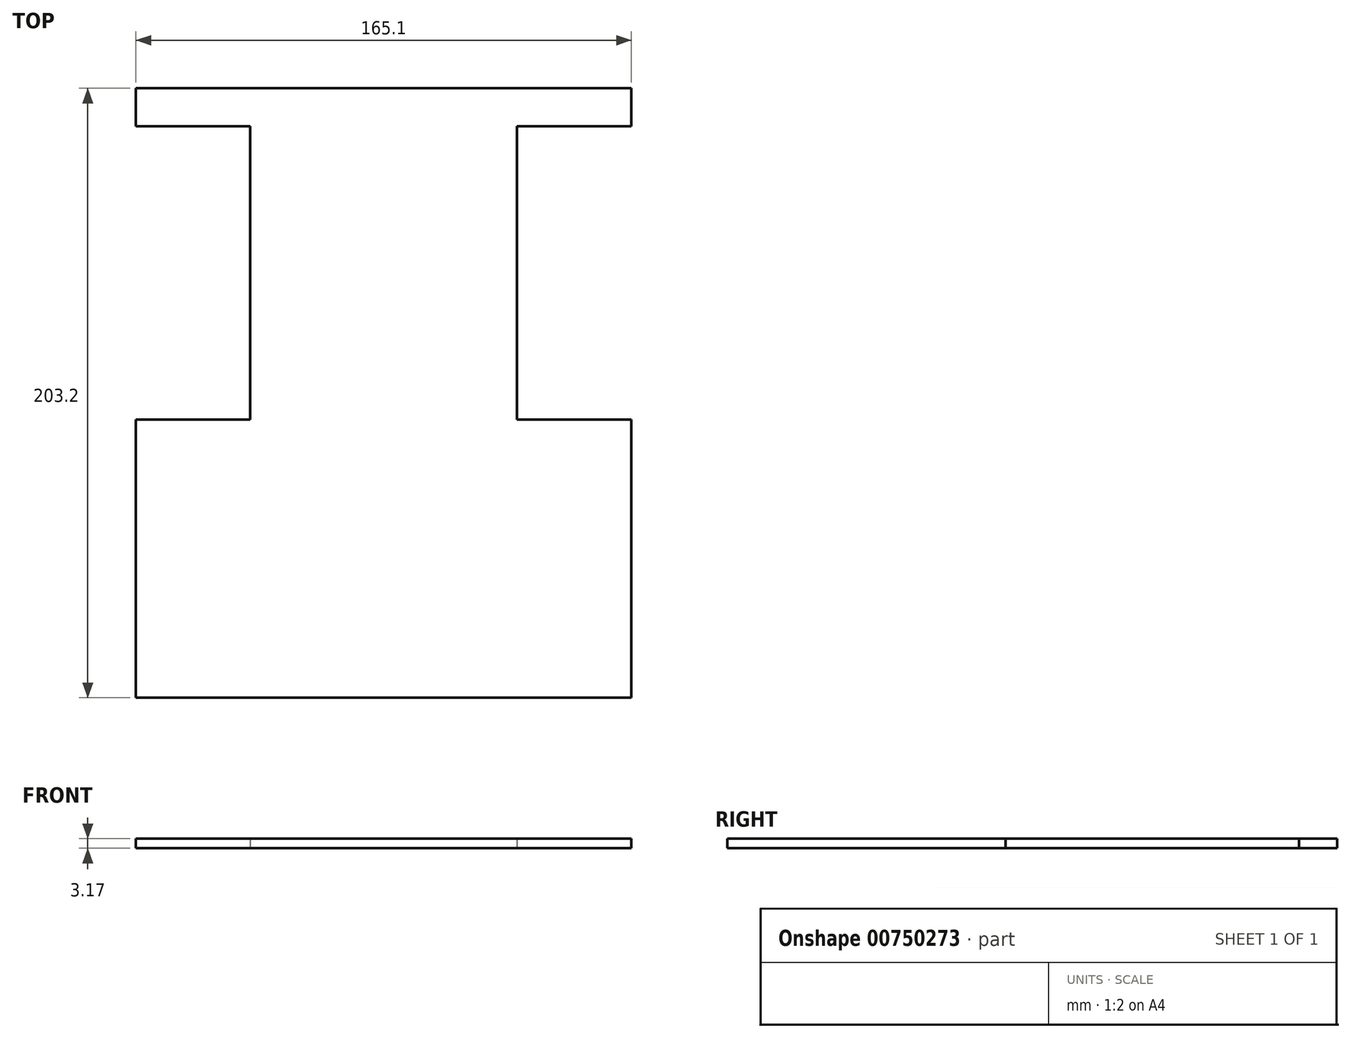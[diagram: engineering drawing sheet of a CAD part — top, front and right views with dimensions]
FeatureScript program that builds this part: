
annotation { "Feature Type Name" : "Feature", "Feature Type Description" : "" }
export const myFeature = defineFeature(function(context is Context, id is Id, definition is map)
    precondition{}
    {
        {
            var Q0;
            Q0=qCreatedBy(makeId("Top.planeOp"),FACE);
            var sketch = newSketch(context, id + "F0", { "sketchPlane" : qUnion([Q0])});
            skLineSegment(sketch, "E0", {"start": v(-55.1, 58.7) * mm, "end": v(-38.1, 58.7) * mm});
            skLineSegment(sketch, "E1", {"start": v(-38.1, 58.7) * mm, "end": v(-38.1, -21.3) * mm});
            skLineSegment(sketch, "E2", {"start": v(-38.1, -21.3) * mm, "end": v(-55.1, -21.3) * mm});
            skLineSegment(sketch, "E3", {"start": v(-55.1, -21.3) * mm, "end": v(-55.1, 58.7) * mm});
            skLineSegment(sketch, "E4", {"start": v(-38.1, 51.4) * mm, "end": v(-38.1, -46.4) * mm});
            skLineSegment(sketch, "E5", {"start": v(-38.1, -46.4) * mm, "end": v(0, -46.4) * mm});
            skLineSegment(sketch, "E6", {"start": v(-38.1, 51.4) * mm, "end": v(0, 51.4) * mm});
            skLineSegment(sketch, "E7", {"start": v(0, 51.4) * mm, "end": v(0, -46.4) * mm});
            skLineSegment(sketch, "E8", {"start": v(-38.1, 58.7) * mm, "end": v(-38.1, 18.7) * mm});
            skLineSegment(sketch, "E9", {"start": v(-38.1, 51.4) * mm, "end": v(-38.1, 18.7) * mm});
            skLineSegment(sketch, "E10", {"start": v(0, 24.96) * mm, "end": v(17, 24.96) * mm});
            skLineSegment(sketch, "E11", {"start": v(17, 24.96) * mm, "end": v(17, 1.94) * mm});
            skLineSegment(sketch, "E12", {"start": v(17, 1.94) * mm, "end": v(0, 1.94) * mm});
            skLineSegment(sketch, "E13", {"start": v(0, 1.94) * mm, "end": v(0, 24.96) * mm});
            skLineSegment(sketch, "E14.MirrorCS", {"start": v(127, 58.7) * mm, "end": v(127, 18.7) * mm});
            skLineSegment(sketch, "E15.MirrorCS", {"start": v(88.9, 24.96) * mm, "end": v(71.9, 24.96) * mm});
            skLineSegment(sketch, "E16.MirrorCS", {"start": v(127, 51.4) * mm, "end": v(127, 18.7) * mm});
            skLineSegment(sketch, "E17.MirrorCS", {"start": v(88.9, 1.94) * mm, "end": v(88.9, 24.96) * mm});
            skLineSegment(sketch, "E18.MirrorCS", {"start": v(127, -46.4) * mm, "end": v(88.9, -46.4) * mm});
            skLineSegment(sketch, "E19.MirrorCS", {"start": v(127, 58.7) * mm, "end": v(127, -21.3) * mm});
            skLineSegment(sketch, "E20.MirrorCS", {"start": v(144, 58.7) * mm, "end": v(127, 58.7) * mm});
            skLineSegment(sketch, "E21.MirrorCS", {"start": v(71.9, 24.96) * mm, "end": v(71.9, 1.94) * mm});
            skLineSegment(sketch, "E22.MirrorCS", {"start": v(144, -21.3) * mm, "end": v(144, 58.7) * mm});
            skLineSegment(sketch, "E23.MirrorCS", {"start": v(127, 51.4) * mm, "end": v(127, -46.4) * mm});
            skLineSegment(sketch, "E24.MirrorCS", {"start": v(88.9, 51.4) * mm, "end": v(88.9, -46.4) * mm});
            skLineSegment(sketch, "E25.MirrorCS", {"start": v(127, 51.4) * mm, "end": v(88.9, 51.4) * mm});
            skLineSegment(sketch, "E26.MirrorCS", {"start": v(127, -21.3) * mm, "end": v(144, -21.3) * mm});
            skLineSegment(sketch, "E27.MirrorCS", {"start": v(71.9, 1.94) * mm, "end": v(88.9, 1.94) * mm});
            skLineSegment(sketch, "E28", {"start": v(-38.1, 51.4) * mm, "end": v(-38.1, 64.1) * mm});
            skLineSegment(sketch, "E29", {"start": v(-38.1, 64.1) * mm, "end": v(127, 64.1) * mm});
            skLineSegment(sketch, "E30", {"start": v(127, 64.1) * mm, "end": v(127, -139.1) * mm});
            skLineSegment(sketch, "E31", {"start": v(127, -139.1) * mm, "end": v(-38.1, -139.1) * mm});
            skLineSegment(sketch, "E32", {"start": v(-38.1, -139.1) * mm, "end": v(-38.1, 64.1) * mm});
            skLineSegment(sketch, "E33", {"start": v(127, -126.4) * mm, "end": v(76.2, -126.4) * mm});
            skLineSegment(sketch, "E34", {"start": v(76.2, -126.4) * mm, "end": v(76.2, -101) * mm});
            skLineSegment(sketch, "E35", {"start": v(76.2, -101) * mm, "end": v(127, -101) * mm});
            skLineSegment(sketch, "E36", {"start": v(127, -101) * mm, "end": v(127, -126.4) * mm});
            skLineSegment(sketch, "E37", {"start": v(-38.1, -126.4) * mm, "end": v(12.7, -126.4) * mm});
            skLineSegment(sketch, "E38", {"start": v(12.7, -126.4) * mm, "end": v(12.7, -101) * mm});
            skLineSegment(sketch, "E39", {"start": v(12.7, -101) * mm, "end": v(-38.1, -101) * mm});
            skLineSegment(sketch, "E40", {"start": v(-38.1, -101) * mm, "end": v(-38.1, -126.4) * mm});
            skLineSegment(sketch, "E41", {"start": v(127, -113.7) * mm, "end": v(127, -73.7) * mm});
            skLineSegment(sketch, "E42", {"start": v(127, -73.7) * mm, "end": v(144, -73.7) * mm});
            skLineSegment(sketch, "E43", {"start": v(144, -73.7) * mm, "end": v(144, -153.7) * mm});
            skLineSegment(sketch, "E44", {"start": v(144, -153.7) * mm, "end": v(127, -153.7) * mm});
            skLineSegment(sketch, "E45", {"start": v(127, -153.7) * mm, "end": v(127, -113.7) * mm});
            skLineSegment(sketch, "E46", {"start": v(-38.1, -113.7) * mm, "end": v(-38.1, -73.7) * mm});
            skLineSegment(sketch, "E47", {"start": v(-38.1, -73.7) * mm, "end": v(-55.1, -73.7) * mm});
            skLineSegment(sketch, "E48", {"start": v(-55.1, -73.7) * mm, "end": v(-55.1, -153.7) * mm});
            skLineSegment(sketch, "E49", {"start": v(-55.1, -153.7) * mm, "end": v(-38.1, -153.7) * mm});
            skLineSegment(sketch, "E50", {"start": v(-38.1, -153.7) * mm, "end": v(-38.1, -113.7) * mm});
            skSolve(sketch);
        }
        {
            var Q0;
            {var subQ10=sQuery(id+"F0.wireOp",EDGE,"E5");Q0=makeQuery(id+"F0.imprint","IMPRINT",FACE,{"disambiguationData":[TD([[makeQuery(id+"F0.imprint","IMPRINT",EDGE,{"derivedFrom":subQ10}),-1.0]])]});}
            var Q1;
            {var subQ0=sQuery(id+"F0.wireOp",EDGE,"E15.MirrorCS");Q1=makeQuery(id+"F0.imprint","IMPRINT",FACE,{"disambiguationData":[TD([[makeQuery(id+"F0.imprint","IMPRINT",EDGE,{"derivedFrom":subQ0}),1.0]])]});}
            var Q2;
            Q2=makeQuery(id+"F0.imprint","IMPRINT",FACE,{"disambiguationData":[TD([[makeQuery(id+"F0.imprint","IMPRINT",EDGE,{"derivedFrom":sQuery(id+"F0.wireOp",EDGE,"E10")}),-1.0]])]});
            var Q3;
            {var subQ4=sQuery(id+"F0.wireOp",EDGE,"E37");Q3=makeQuery(id+"F0.imprint","IMPRINT",FACE,{"disambiguationData":[TD([[makeQuery(id+"F0.imprint","IMPRINT",EDGE,{"derivedFrom":subQ4}),1.0]])]});}
            var Q4;
            {var subQ2=sQuery(id+"F0.wireOp",EDGE,"E33");Q4=makeQuery(id+"F0.imprint","IMPRINT",FACE,{"disambiguationData":[TD([[makeQuery(id+"F0.imprint","IMPRINT",EDGE,{"derivedFrom":subQ2}),-1.0]])]});}
            extrude(context, id + "F1", {"entities" : qUnion([Q0, Q1, Q2, Q3, Q4]), "depth" : 3.17 * mm, "offsetDistance" : 25.4 * mm});
        }
    });
